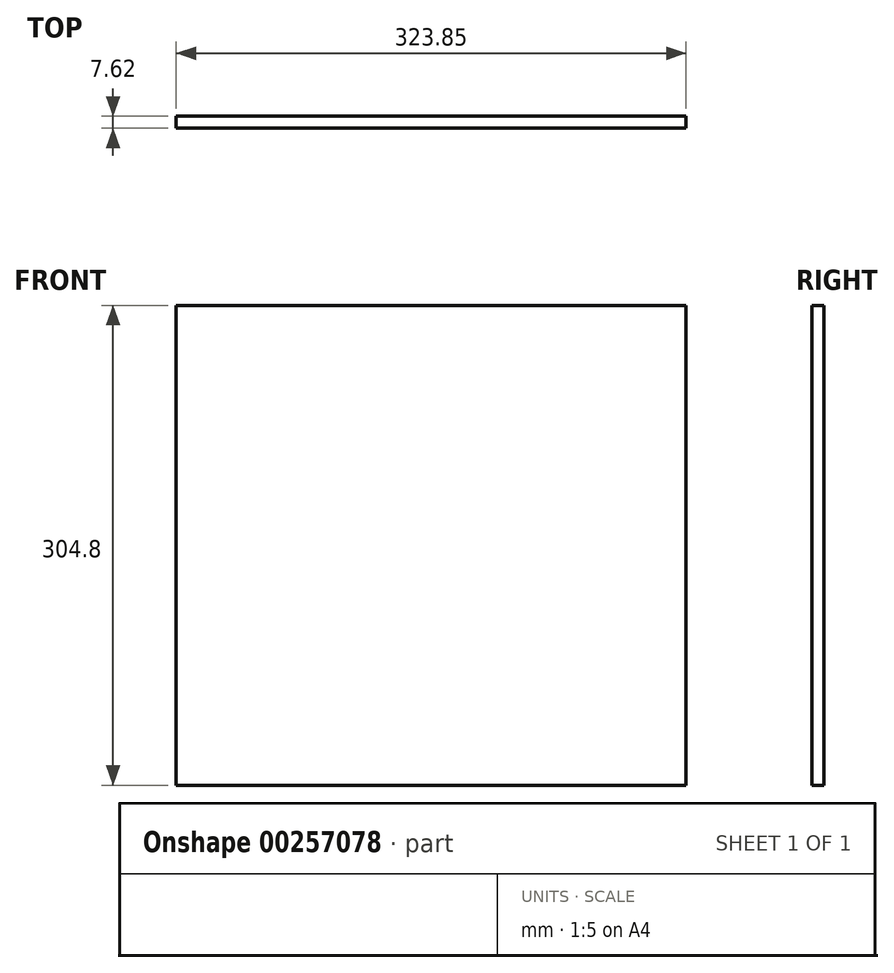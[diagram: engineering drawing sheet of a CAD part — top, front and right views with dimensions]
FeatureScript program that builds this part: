
annotation { "Feature Type Name" : "Feature", "Feature Type Description" : "" }
export const myFeature = defineFeature(function(context is Context, id is Id, definition is map)
    precondition{}
    {
        {
            var Q0;
            Q0=qCreatedBy(makeId("Front.planeOp"),FACE);
            var sketch = newSketch(context, id + "F0", { "sketchPlane" : qUnion([Q0])});
            skLineSegment(sketch, "E0.bottom", {"start": v(-53.3, 218.21) * mm, "end": v(270.56, 218.21) * mm});
            skLineSegment(sketch, "E0.top", {"start": v(-53.3, -86.59) * mm, "end": v(270.56, -86.59) * mm});
            skLineSegment(sketch, "E0.left", {"start": v(-53.3, 218.21) * mm, "end": v(-53.3, -86.59) * mm});
            skLineSegment(sketch, "E0.right", {"start": v(270.56, 218.21) * mm, "end": v(270.56, -86.59) * mm});
            skSolve(sketch);
        }
        {
            var Q0;
            Q0=makeQuery(id+"F0.imprint","IMPRINT",FACE,{"disambiguationData":[TD([[makeQuery(id+"F0.imprint","IMPRINT",EDGE,{"derivedFrom":sQuery(id+"F0.wireOp",EDGE,"E0.bottom")}),-1.0]])]});
            extrude(context, id + "F1", {"entities" : qUnion([Q0]), "depth" : 7.62 * mm});
        }
    });
